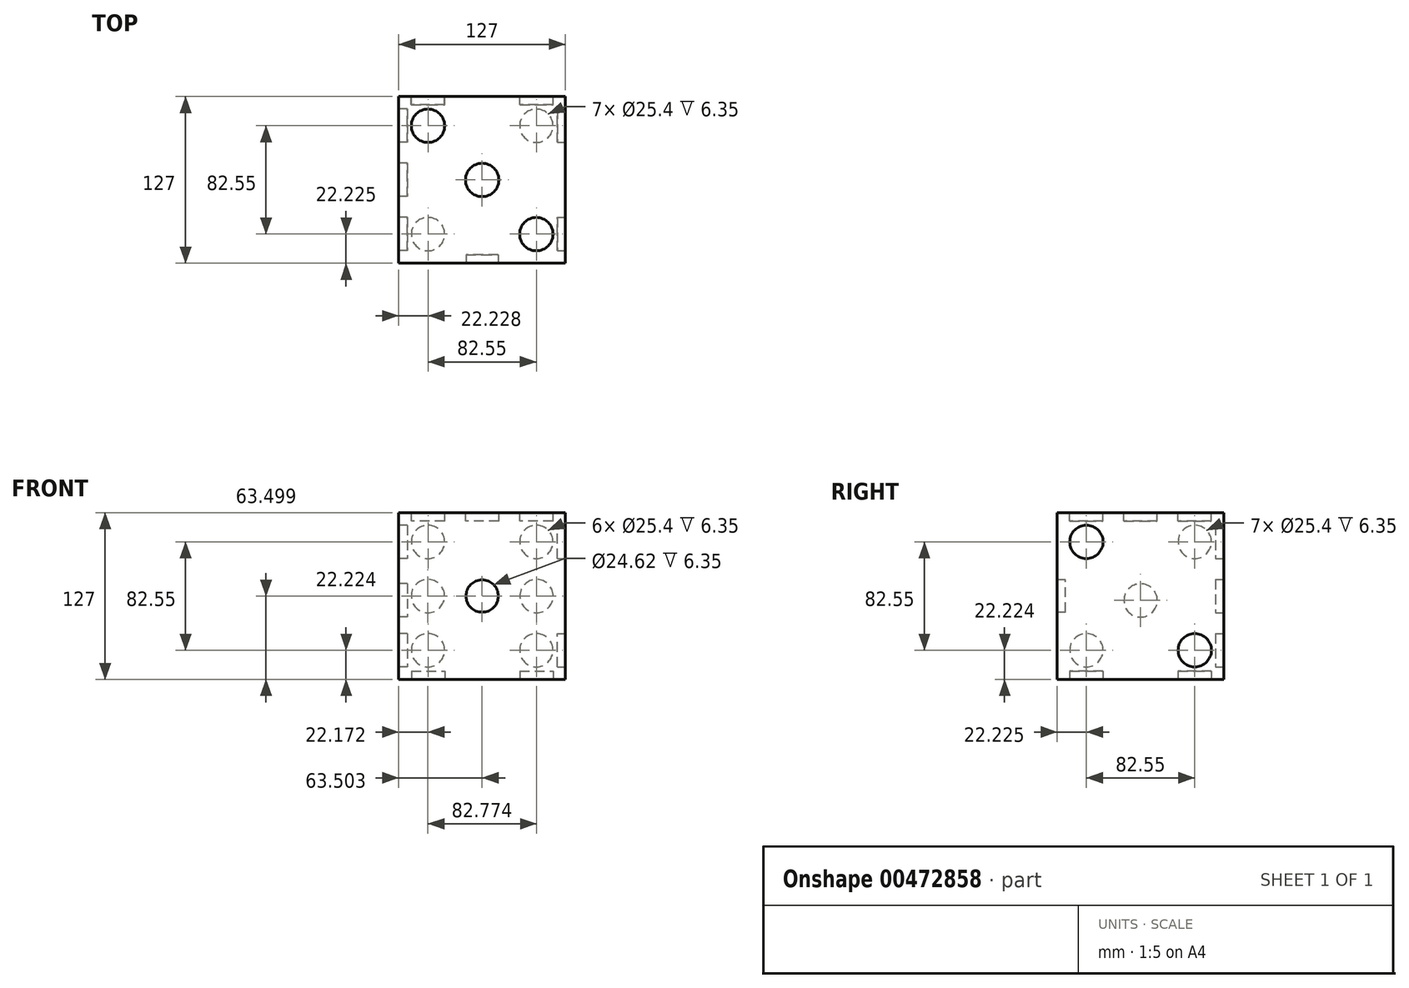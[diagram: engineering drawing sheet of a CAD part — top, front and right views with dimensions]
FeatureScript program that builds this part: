
annotation { "Feature Type Name" : "Feature", "Feature Type Description" : "" }
export const myFeature = defineFeature(function(context is Context, id is Id, definition is map)
    precondition{}
    {
        {
            var Q0;
            Q0=qCreatedBy(makeId("Front.planeOp"),FACE);
            var sketch = newSketch(context, id + "F0", { "sketchPlane" : qUnion([Q0])});
            skLineSegment(sketch, "E0.bottom", {"start": v(-61.52, 66.86) * mm, "end": v(65.48, 66.86) * mm});
            skLineSegment(sketch, "E0.top", {"start": v(-61.52, -60.14) * mm, "end": v(65.48, -60.14) * mm});
            skLineSegment(sketch, "E0.left", {"start": v(-61.52, 66.86) * mm, "end": v(-61.52, -60.14) * mm});
            skLineSegment(sketch, "E0.right", {"start": v(65.48, 66.86) * mm, "end": v(65.48, -60.14) * mm});
            skSolve(sketch);
        }
        {
            var Q0;
            Q0 = qSketchRegion(id + "F0", true);
            extrude(context, id + "F1", {"entities" : qUnion([Q0]), "depth" : 127 * mm});
        }
        {
            var Q0;
            Q0=makeQuery(id+"F1.opExtrude","CAP_FACE",FACE,{"disambiguationData":[OSD([sQuery(id+"F0.wireOp",EDGE,"E0.bottom"),sQuery(id+"F0.wireOp",EDGE,"E0.top"),sQuery(id+"F0.wireOp",EDGE,"E0.left"),sQuery(id+"F0.wireOp",EDGE,"E0.right")])],"isStart":false});
            var sketch = newSketch(context, id + "F2", { "sketchPlane" : qUnion([Q0])});
            skCircle(sketch, "E1", {"center": v(1.98, 3.36) * mm, "radius": 12.31 * mm});
            skPoint(sketch, "E1.centerSnap0", {"position": v(1.98, 66.86) * mm});
            skPoint(sketch, "E1.centerSnap1", {"position": v(-61.52, 3.36) * mm});
            skSolve(sketch);
        }
        {
            var Q0;
            Q0=makeQuery(id+"F2.imprint","IMPRINT",FACE,{"disambiguationData":[TD([[makeQuery(id+"F2.imprint","IMPRINT",EDGE,{"derivedFrom":sQuery(id+"F2.wireOp",EDGE,"E1")}),1.0]])]});
            extrude(context, id + "F3", {"entities" : qUnion([Q0]), "operationType" : NewBodyOperationType.REMOVE, "oppositeDirection" : true, "depth" : 6.35 * mm});
        }
        {
            var Q0;
            Q0=makeQuery(id+"F1.opExtrude","CAP_FACE",FACE,{"disambiguationData":[OSD([sQuery(id+"F0.wireOp",EDGE,"E0.bottom"),sQuery(id+"F0.wireOp",EDGE,"E0.top"),sQuery(id+"F0.wireOp",EDGE,"E0.left"),sQuery(id+"F0.wireOp",EDGE,"E0.right")])],"isStart":true});
            var sketch = newSketch(context, id + "F4", { "sketchPlane" : qUnion([Q0])});
            skCircle(sketch, "E2", {"center": v(-43.26, 44.63) * mm, "radius": 12.7 * mm});
            skCircle(sketch, "E3", {"center": v(-43.26, -37.92) * mm, "radius": 12.7 * mm});
            skCircle(sketch, "E4", {"center": v(39.3, -37.92) * mm, "radius": 12.7 * mm});
            skCircle(sketch, "E5", {"center": v(39.3, 44.63) * mm, "radius": 12.7 * mm});
            skCircle(sketch, "E6", {"center": v(-43.43, 3.36) * mm, "radius": 12.7 * mm});
            skCircle(sketch, "E7", {"center": v(39.35, 3.36) * mm, "radius": 12.7 * mm});
            skSolve(sketch);
        }
        {
            var Q0;
            Q0=makeQuery(id+"F4.imprint","IMPRINT",FACE,{"disambiguationData":[TD([[makeQuery(id+"F4.imprint","IMPRINT",EDGE,{"derivedFrom":sQuery(id+"F4.wireOp",EDGE,"E4")}),1.0]])]});
            var Q1;
            Q1=makeQuery(id+"F4.imprint","IMPRINT",FACE,{"disambiguationData":[TD([[makeQuery(id+"F4.imprint","IMPRINT",EDGE,{"derivedFrom":sQuery(id+"F4.wireOp",EDGE,"E7")}),1.0]])]});
            var Q2;
            Q2=makeQuery(id+"F4.imprint","IMPRINT",FACE,{"disambiguationData":[TD([[makeQuery(id+"F4.imprint","IMPRINT",EDGE,{"derivedFrom":sQuery(id+"F4.wireOp",EDGE,"E5")}),1.0]])]});
            var Q3;
            Q3=makeQuery(id+"F4.imprint","IMPRINT",FACE,{"disambiguationData":[TD([[makeQuery(id+"F4.imprint","IMPRINT",EDGE,{"derivedFrom":sQuery(id+"F4.wireOp",EDGE,"E2")}),1.0]])]});
            var Q4;
            Q4=makeQuery(id+"F4.imprint","IMPRINT",FACE,{"disambiguationData":[TD([[makeQuery(id+"F4.imprint","IMPRINT",EDGE,{"derivedFrom":sQuery(id+"F4.wireOp",EDGE,"E3")}),1.0]])]});
            var Q5;
            Q5=makeQuery(id+"F4.imprint","IMPRINT",FACE,{"disambiguationData":[TD([[makeQuery(id+"F4.imprint","IMPRINT",EDGE,{"derivedFrom":sQuery(id+"F4.wireOp",EDGE,"E6")}),1.0]])]});
            extrude(context, id + "F5", {"entities" : qUnion([Q0, Q1, Q2, Q3, Q4, Q5]), "operationType" : NewBodyOperationType.REMOVE, "oppositeDirection" : true, "depth" : 6.35 * mm});
        }
        {
            var Q0;
            Q0=makeQuery(id+"F1.opExtrude","SWEPT_FACE",FACE,{"disambiguationData":[OSD([sQuery(id+"F0.wireOp",EDGE,"E0.right")])]});
            var sketch = newSketch(context, id + "F6", { "sketchPlane" : qUnion([Q0])});
            skCircle(sketch, "E8", {"center": v(-104.78, 44.63) * mm, "radius": 12.7 * mm});
            skCircle(sketch, "E9", {"center": v(-22.23, -37.92) * mm, "radius": 12.7 * mm});
            skSolve(sketch);
        }
        {
            var Q0;
            Q0=makeQuery(id+"F6.imprint","IMPRINT",FACE,{"disambiguationData":[TD([[makeQuery(id+"F6.imprint","IMPRINT",EDGE,{"derivedFrom":sQuery(id+"F6.wireOp",EDGE,"E9")}),1.0]])]});
            var Q1;
            Q1=makeQuery(id+"F6.imprint","IMPRINT",FACE,{"disambiguationData":[TD([[makeQuery(id+"F6.imprint","IMPRINT",EDGE,{"derivedFrom":sQuery(id+"F6.wireOp",EDGE,"E8")}),1.0]])]});
            extrude(context, id + "F7", {"entities" : qUnion([Q0, Q1]), "operationType" : NewBodyOperationType.REMOVE, "oppositeDirection" : true, "depth" : 6.35 * mm});
        }
        {
            var Q0;
            Q0=makeQuery(id+"F1.opExtrude","SWEPT_FACE",FACE,{"disambiguationData":[OSD([sQuery(id+"F0.wireOp",EDGE,"E0.left")])]});
            var sketch = newSketch(context, id + "F8", { "sketchPlane" : qUnion([Q0])});
            skCircle(sketch, "E10", {"center": v(22.23, 44.63) * mm, "radius": 12.7 * mm});
            skCircle(sketch, "E11", {"center": v(104.78, 44.63) * mm, "radius": 12.7 * mm});
            skCircle(sketch, "E12", {"center": v(104.78, -37.92) * mm, "radius": 12.7 * mm});
            skCircle(sketch, "E13", {"center": v(22.23, -37.92) * mm, "radius": 12.7 * mm});
            skCircle(sketch, "E14", {"center": v(63.5, 0) * mm, "radius": 12.7 * mm});
            skPoint(sketch, "E14.centerSnap0", {"position": v(63.5, 66.86) * mm});
            skSolve(sketch);
        }
        {
            var Q0;
            Q0 = qSketchRegion(id + "F8", true);
            extrude(context, id + "F9", {"entities" : qUnion([Q0]), "operationType" : NewBodyOperationType.REMOVE, "oppositeDirection" : true, "depth" : 6.35 * mm});
        }
        {
            var Q0;
            Q0=makeQuery(id+"F1.opExtrude","SWEPT_FACE",FACE,{"disambiguationData":[OSD([sQuery(id+"F0.wireOp",EDGE,"E0.top")])]});
            var sketch = newSketch(context, id + "F10", { "sketchPlane" : qUnion([Q0])});
            skCircle(sketch, "E15", {"center": v(-39.3, 104.78) * mm, "radius": 12.7 * mm});
            skCircle(sketch, "E16", {"center": v(43.26, 104.78) * mm, "radius": 12.7 * mm});
            skCircle(sketch, "E17", {"center": v(-39.3, 22.22) * mm, "radius": 12.7 * mm});
            skCircle(sketch, "E18", {"center": v(43.26, 22.22) * mm, "radius": 12.7 * mm});
            skSolve(sketch);
        }
        {
            var Q0;
            Q0 = qSketchRegion(id + "F10", true);
            extrude(context, id + "F11", {"entities" : qUnion([Q0]), "operationType" : NewBodyOperationType.REMOVE, "oppositeDirection" : true, "depth" : 6.35 * mm});
        }
        {
            var Q0;
            Q0=makeQuery(id+"F1.opExtrude","SWEPT_FACE",FACE,{"disambiguationData":[OSD([sQuery(id+"F0.wireOp",EDGE,"E0.bottom")])]});
            var sketch = newSketch(context, id + "F12", { "sketchPlane" : qUnion([Q0])});
            skCircle(sketch, "E19", {"center": v(-39.3, -22.22) * mm, "radius": 12.7 * mm});
            skCircle(sketch, "E20", {"center": v(43.26, -104.78) * mm, "radius": 12.7 * mm});
            skCircle(sketch, "E21", {"center": v(1.98, -63.5) * mm, "radius": 12.7 * mm});
            skPoint(sketch, "E21.centerSnap0", {"position": v(-61.52, -63.5) * mm});
            skPoint(sketch, "E21.centerSnap1", {"position": v(1.98, 0) * mm});
            skSolve(sketch);
        }
        {
            var Q0;
            Q0 = qSketchRegion(id + "F12", true);
            extrude(context, id + "F13", {"entities" : qUnion([Q0]), "operationType" : NewBodyOperationType.REMOVE, "oppositeDirection" : true, "depth" : 6.35 * mm});
        }
    });
